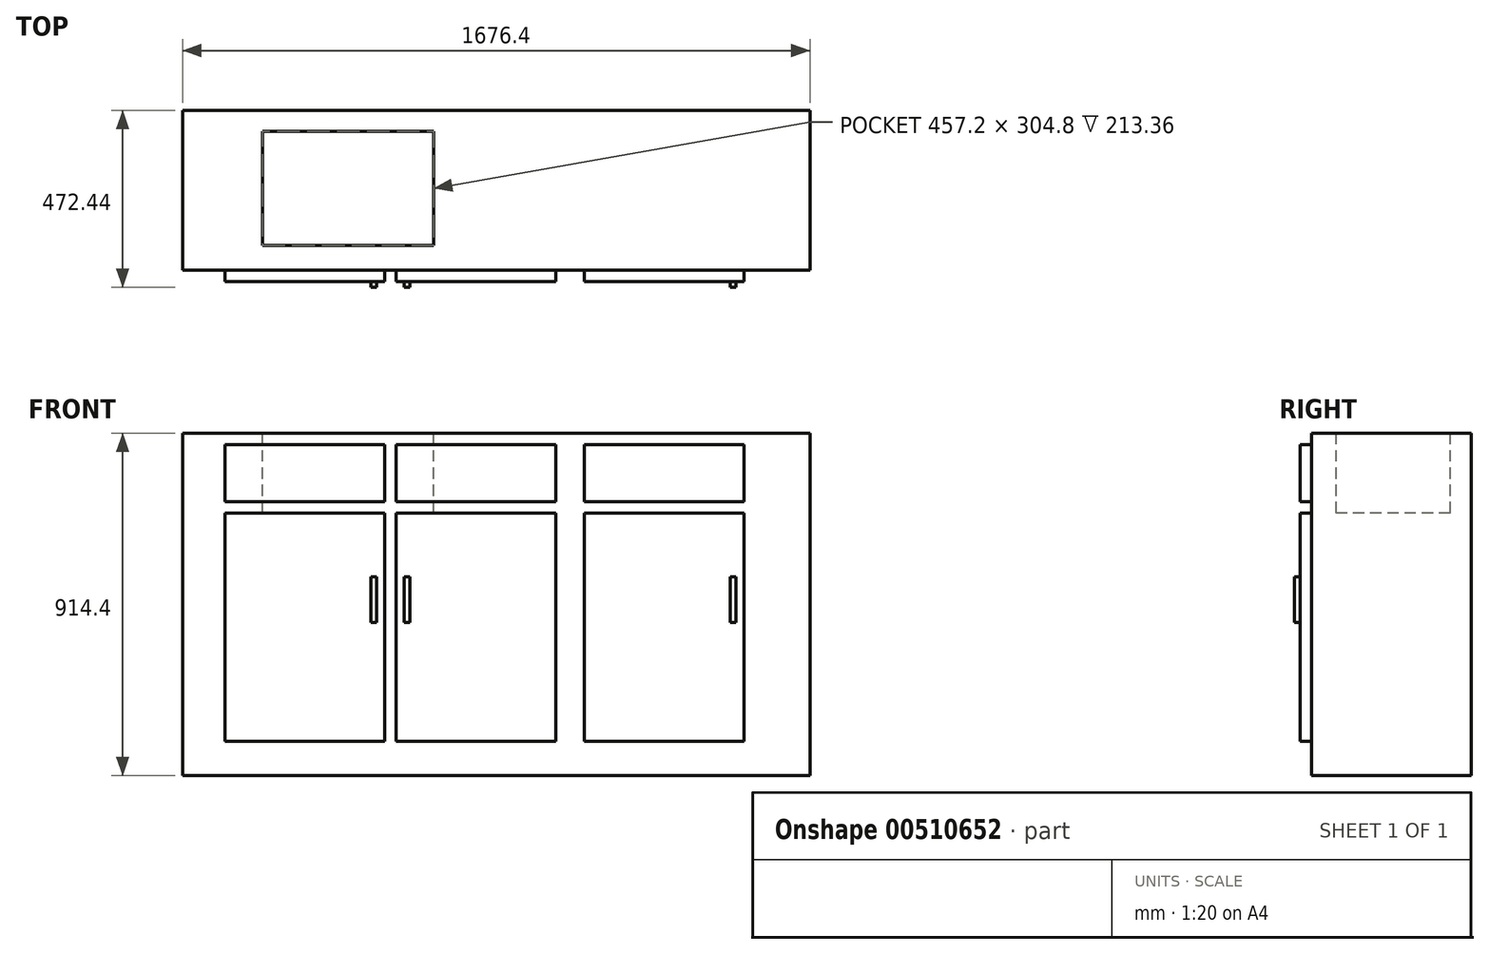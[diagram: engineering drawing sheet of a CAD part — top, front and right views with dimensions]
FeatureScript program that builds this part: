
annotation { "Feature Type Name" : "Feature", "Feature Type Description" : "" }
export const myFeature = defineFeature(function(context is Context, id is Id, definition is map)
    precondition{}
    {
        {
            var Q0;
            Q0=qCreatedBy(makeId("Front.planeOp"),FACE);
            var sketch = newSketch(context, id + "F0", { "sketchPlane" : qUnion([Q0])});
            skLineSegment(sketch, "E0", {"start": v(-838.2, 505.49) * mm, "end": v(-838.2, -408.91) * mm});
            skLineSegment(sketch, "E1", {"start": v(-838.2, -408.91) * mm, "end": v(838.2, -408.91) * mm});
            skLineSegment(sketch, "E2", {"start": v(838.2, -408.91) * mm, "end": v(838.2, 505.49) * mm});
            skLineSegment(sketch, "E3", {"start": v(-838.2, 505.49) * mm, "end": v(838.2, 505.49) * mm});
            skSolve(sketch);
        }
        {
            var Q0;
            Q0 = qSketchRegion(id + "F0", true);
            extrude(context, id + "F1", {"entities" : qUnion([Q0]), "depth" : 426.72 * mm, "offsetDistance" : 30.48 * mm});
        }
        {
            var Q0;
            Q0=makeQuery(id+"F1.opExtrude","CAP_FACE",FACE,{"disambiguationData":[OSD([sQuery(id+"F0.wireOp",EDGE,"E0"),sQuery(id+"F0.wireOp",EDGE,"E1"),sQuery(id+"F0.wireOp",EDGE,"E2"),sQuery(id+"F0.wireOp",EDGE,"E3")])],"isStart":false});
            var sketch = newSketch(context, id + "F2", { "sketchPlane" : qUnion([Q0])});
            skLineSegment(sketch, "E4", {"start": v(-724.92, 292.13) * mm, "end": v(-298.2, 292.13) * mm});
            skLineSegment(sketch, "E5", {"start": v(-298.2, 292.13) * mm, "end": v(-298.2, -317.47) * mm});
            skLineSegment(sketch, "E6", {"start": v(-298.2, -317.47) * mm, "end": v(-724.92, -317.47) * mm});
            skLineSegment(sketch, "E7", {"start": v(-724.92, -317.47) * mm, "end": v(-724.92, 292.13) * mm});
            skLineSegment(sketch, "E8", {"start": v(-267.72, 292.13) * mm, "end": v(159, 292.13) * mm});
            skLineSegment(sketch, "E9", {"start": v(159, 292.13) * mm, "end": v(159, -317.47) * mm});
            skLineSegment(sketch, "E10", {"start": v(159, -317.47) * mm, "end": v(-267.72, -317.47) * mm});
            skLineSegment(sketch, "E11", {"start": v(-267.72, -317.47) * mm, "end": v(-267.72, 292.13) * mm});
            skLineSegment(sketch, "E12", {"start": v(235.2, 292.13) * mm, "end": v(661.92, 292.13) * mm});
            skLineSegment(sketch, "E13", {"start": v(661.92, 292.13) * mm, "end": v(661.92, -317.47) * mm});
            skLineSegment(sketch, "E14", {"start": v(661.92, -317.47) * mm, "end": v(235.2, -317.47) * mm});
            skLineSegment(sketch, "E15", {"start": v(235.2, -317.47) * mm, "end": v(235.2, 292.13) * mm});
            skLineSegment(sketch, "E16.bottom", {"start": v(-724.92, 475) * mm, "end": v(-298.2, 475) * mm});
            skLineSegment(sketch, "E16.top", {"start": v(-724.92, 322.6) * mm, "end": v(-298.2, 322.6) * mm});
            skLineSegment(sketch, "E16.left", {"start": v(-724.92, 475) * mm, "end": v(-724.92, 322.6) * mm});
            skLineSegment(sketch, "E16.right", {"start": v(-298.2, 475) * mm, "end": v(-298.2, 322.6) * mm});
            skLineSegment(sketch, "E17.bottom", {"start": v(-267.72, 322.6) * mm, "end": v(159, 322.6) * mm});
            skLineSegment(sketch, "E17.top", {"start": v(-267.72, 475) * mm, "end": v(159, 475) * mm});
            skLineSegment(sketch, "E17.left", {"start": v(-267.72, 322.6) * mm, "end": v(-267.72, 475) * mm});
            skLineSegment(sketch, "E17.right", {"start": v(159, 322.6) * mm, "end": v(159, 475) * mm});
            skLineSegment(sketch, "E18.bottom", {"start": v(235.2, 475) * mm, "end": v(661.92, 475) * mm});
            skLineSegment(sketch, "E18.top", {"start": v(235.2, 322.6) * mm, "end": v(661.92, 322.6) * mm});
            skLineSegment(sketch, "E18.left", {"start": v(235.2, 475) * mm, "end": v(235.2, 322.6) * mm});
            skLineSegment(sketch, "E18.right", {"start": v(661.92, 475) * mm, "end": v(661.92, 322.6) * mm});
            skSolve(sketch);
        }
        {
            var Q0;
            Q0 = qSketchRegion(id + "F2", true);
            extrude(context, id + "F3", {"entities" : qUnion([Q0]), "operationType" : NewBodyOperationType.ADD, "depth" : 30.48 * mm, "offsetDistance" : 30.48 * mm});
        }
        {
            var Q0;
            Q0=makeQuery(id+"F1.opExtrude","CAP_FACE",FACE,{"disambiguationData":[OSD([sQuery(id+"F0.wireOp",EDGE,"E0"),sQuery(id+"F0.wireOp",EDGE,"E1"),sQuery(id+"F0.wireOp",EDGE,"E2"),sQuery(id+"F0.wireOp",EDGE,"E3")])],"isStart":false});
            var sketch = newSketch(context, id + "F4", { "sketchPlane" : qUnion([Q0])});
            skLineSegment(sketch, "E19", {"start": v(-334.78, 121.92) * mm, "end": v(-334.78, 0) * mm});
            skLineSegment(sketch, "E20", {"start": v(-334.78, 0) * mm, "end": v(-319.54, 0) * mm});
            skLineSegment(sketch, "E21", {"start": v(-319.54, 0) * mm, "end": v(-319.54, 121.92) * mm});
            skLineSegment(sketch, "E22", {"start": v(-319.54, 121.92) * mm, "end": v(-334.78, 121.92) * mm});
            skLineSegment(sketch, "E23.bottom", {"start": v(-246.39, 121.92) * mm, "end": v(-231.15, 121.92) * mm});
            skLineSegment(sketch, "E23.top", {"start": v(-246.39, 0) * mm, "end": v(-231.15, 0) * mm});
            skLineSegment(sketch, "E23.left", {"start": v(-246.39, 121.92) * mm, "end": v(-246.39, 0) * mm});
            skLineSegment(sketch, "E23.right", {"start": v(-231.15, 121.92) * mm, "end": v(-231.15, 0) * mm});
            skLineSegment(sketch, "E24.bottom", {"start": v(625.34, 122.05) * mm, "end": v(640.58, 122.05) * mm});
            skLineSegment(sketch, "E24.top", {"start": v(625.34, 0.13) * mm, "end": v(640.58, 0.13) * mm});
            skLineSegment(sketch, "E24.left", {"start": v(625.34, 122.05) * mm, "end": v(625.34, 0.13) * mm});
            skLineSegment(sketch, "E24.right", {"start": v(640.58, 122.05) * mm, "end": v(640.58, 0.13) * mm});
            skSolve(sketch);
        }
        {
            var Q0;
            Q0 = qSketchRegion(id + "F4", true);
            extrude(context, id + "F5", {"entities" : qUnion([Q0]), "operationType" : NewBodyOperationType.ADD, "depth" : 45.72 * mm, "offsetDistance" : 30.48 * mm});
        }
        {
            var Q0;
            Q0=makeQuery(id+"F1.opExtrude","SWEPT_FACE",FACE,{"disambiguationData":[OSD([sQuery(id+"F0.wireOp",EDGE,"E3")])]});
            var sketch = newSketch(context, id + "F6", { "sketchPlane" : qUnion([Q0])});
            skLineSegment(sketch, "E25.bottom", {"start": v(-624.84, -56.48) * mm, "end": v(-167.64, -56.48) * mm});
            skLineSegment(sketch, "E25.top", {"start": v(-624.84, -361.28) * mm, "end": v(-167.64, -361.28) * mm});
            skLineSegment(sketch, "E25.left", {"start": v(-624.84, -56.48) * mm, "end": v(-624.84, -361.28) * mm});
            skLineSegment(sketch, "E25.right", {"start": v(-167.64, -56.48) * mm, "end": v(-167.64, -361.28) * mm});
            skSolve(sketch);
        }
        {
            var Q0;
            Q0 = qSketchRegion(id + "F6", true);
            extrude(context, id + "F7", {"entities" : qUnion([Q0]), "operationType" : NewBodyOperationType.REMOVE, "oppositeDirection" : true, "depth" : 213.36 * mm, "offsetDistance" : 30.48 * mm});
        }
    });
